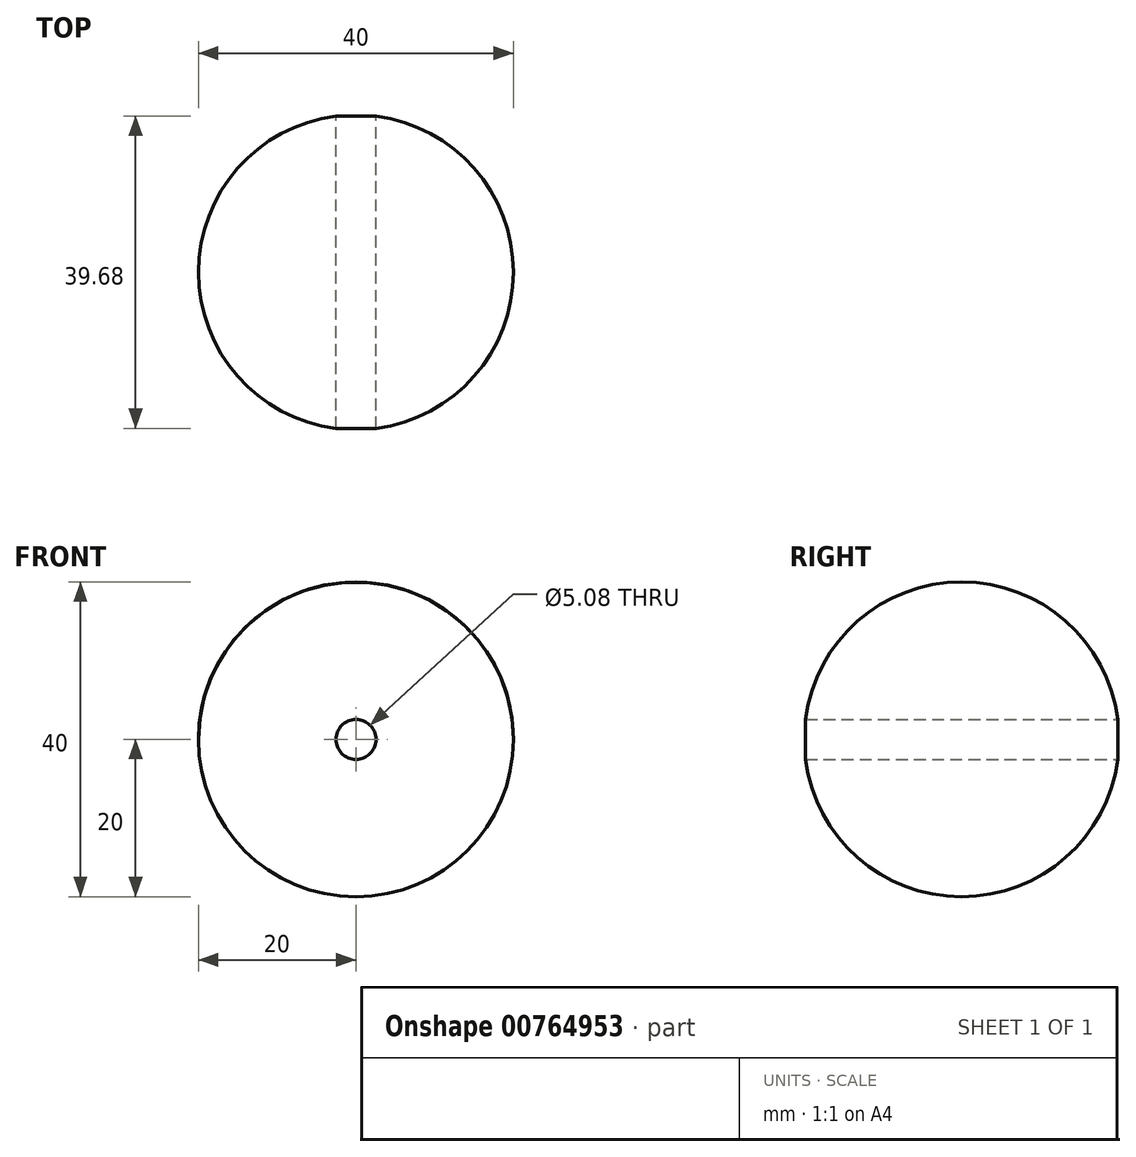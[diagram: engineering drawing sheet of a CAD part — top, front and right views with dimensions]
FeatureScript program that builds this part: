
annotation { "Feature Type Name" : "Feature", "Feature Type Description" : "" }
export const myFeature = defineFeature(function(context is Context, id is Id, definition is map)
    precondition{}
    {
        {
            var Q0;
            Q0=qCreatedBy(makeId("Front.planeOp"),FACE);
            var sketch = newSketch(context, id + "F0", { "sketchPlane" : qUnion([Q0])});
            skArc(sketch, "E0", {"start": v(20, 0) * mm, "mid": v(0, 20) * mm, "end": v(-20, 0) * mm});
            skLineSegment(sketch, "E1", {"start": v(20, 0) * mm, "end": v(-20, 0) * mm});
            skSolve(sketch);
        }
        {
            var Q0;
            Q0=makeQuery(id+"F0.imprint","IMPRINT",FACE,{"disambiguationData":[TD([[makeQuery(id+"F0.imprint","IMPRINT",EDGE,{"derivedFrom":sQuery(id+"F0.wireOp",EDGE,"E0")}),1.0]])]});
            var Q1;
            Q1=sQuery(id+"F0.wireOp",EDGE,"E1");
            revolve(context, id + "F1", {"surfaceOperationType" : NewSurfaceOperationType.NEW, "entities" : qUnion([Q0]), "axis" : qUnion([Q1]), "revolveType" : RevolveType.FULL});
        }
        {
            var Q0;
            Q0=qCreatedBy(makeId("Front.planeOp"),FACE);
            var sketch = newSketch(context, id + "F2", { "sketchPlane" : qUnion([Q0])});
            skCircle(sketch, "E2", {"center": v(0, 0) * mm, "radius": 2.54 * mm});
            skSolve(sketch);
        }
        {
            var Q0;
            Q0 = qSketchRegion(id + "F2", true);
            extrude(context, id + "F3", {"entities" : qUnion([Q0]), "operationType" : NewBodyOperationType.REMOVE, "endBound" : BoundingType.THROUGH_ALL, "depth" : 25.4 * mm, "offsetDistance" : 25.4 * mm, "hasSecondDirection" : true, "secondDirectionBound" : SecondDirectionBoundingType.THROUGH_ALL, "secondDirectionOppositeDirection" : true, "secondDirectionDepth" : 25.4 * mm});
        }
    });
